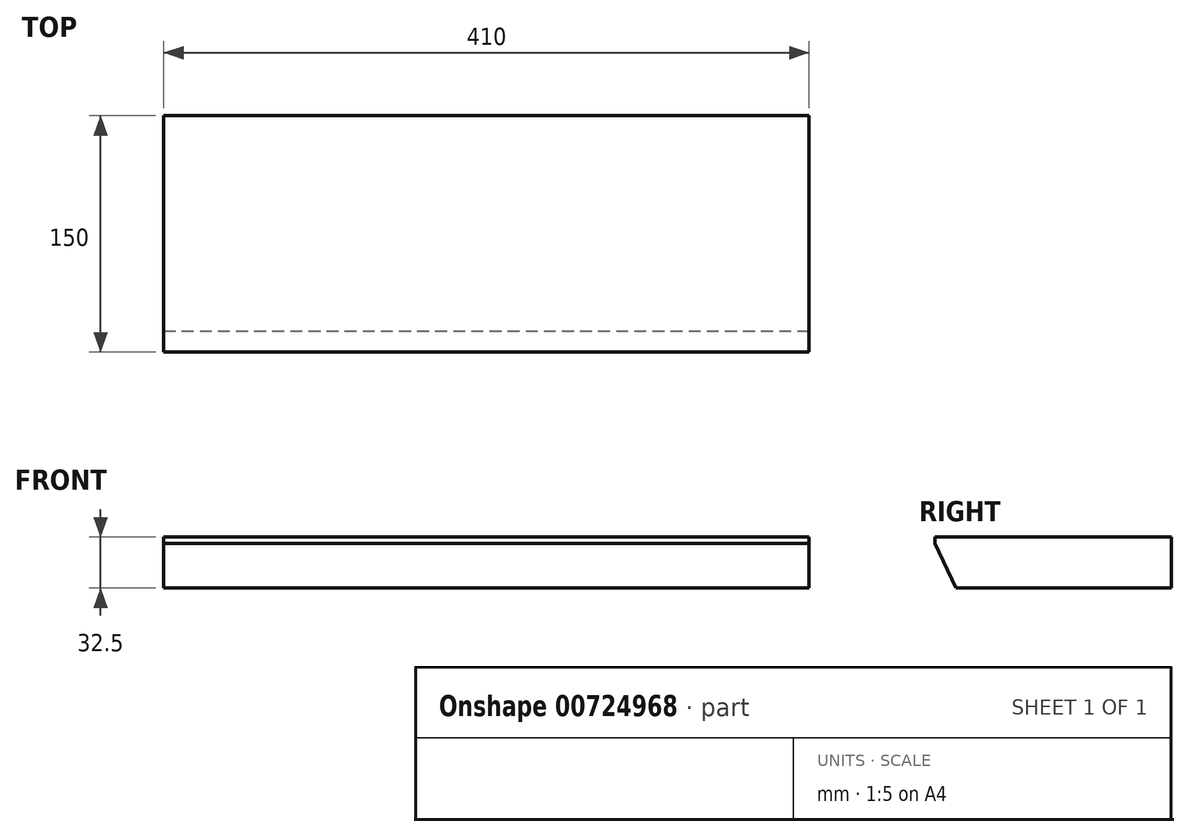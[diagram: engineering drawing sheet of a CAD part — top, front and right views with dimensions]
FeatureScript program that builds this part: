
annotation { "Feature Type Name" : "Feature", "Feature Type Description" : "" }
export const myFeature = defineFeature(function(context is Context, id is Id, definition is map)
    precondition{}
    {
        {
            var Q0;
            Q0=qCreatedBy(makeId("Top.planeOp"),FACE);
            var sketch = newSketch(context, id + "F0", { "sketchPlane" : qUnion([Q0])});
            skLineSegment(sketch, "E0.bottom", {"start": v(205, -75) * mm, "end": v(-205, -75) * mm});
            skLineSegment(sketch, "E0.top", {"start": v(205, 75) * mm, "end": v(-205, 75) * mm});
            skLineSegment(sketch, "E0.left", {"start": v(205, -75) * mm, "end": v(205, 75) * mm});
            skLineSegment(sketch, "E0.right", {"start": v(-205, -75) * mm, "end": v(-205, 75) * mm});
            skPoint(sketch, "E0.middle", {"position": v(0, 0) * mm});
            skSolve(sketch);
        }
        {
            var Q0;
            Q0 = qSketchRegion(id + "F0", true);
            extrude(context, id + "F1", {"entities" : qUnion([Q0]), "depth" : 32.5 * mm, "offsetDistance" : 25 * mm});
        }
        {
            var Q0;
            Q0=makeQuery(id+"F1.opExtrude","SWEPT_FACE",FACE,{"disambiguationData":[OSD([sQuery(id+"F0.wireOp",EDGE,"E0.left")])]});
            var sketch = newSketch(context, id + "F2", { "sketchPlane" : qUnion([Q0])});
            skLineSegment(sketch, "E1.0", {"start": v(-75, 0) * mm, "end": v(75, 0) * mm});
            skLineSegment(sketch, "E2.0", {"start": v(-75, 32.5) * mm, "end": v(-75, 0) * mm});
            skLineSegment(sketch, "E3", {"start": v(-75, 28.5) * mm, "end": v(-61.71, 0) * mm});
            skSolve(sketch);
        }
        {
            var Q0;
            Q0 = qSketchRegion(id + "F2", true);
            extrude(context, id + "F3", {"entities" : qUnion([Q0]), "operationType" : NewBodyOperationType.REMOVE, "endBound" : BoundingType.THROUGH_ALL, "oppositeDirection" : true, "depth" : 25 * mm, "offsetDistance" : 25 * mm});
        }
    });
